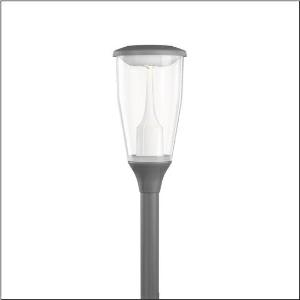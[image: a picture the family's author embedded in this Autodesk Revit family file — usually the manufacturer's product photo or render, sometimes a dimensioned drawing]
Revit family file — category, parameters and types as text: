
# Revit family: dl_11_iq___p1_0a_5xa5575nf14h000022_259a
name_source: partatom
category: Lighting Fixtures
units: mm (PartAtom-declared; Revit-internal decimal feet)

## family parameters
Cut with Voids When Loaded = No
Host = Face
Light Source = No
Part Type = Normal
Room Calculation Point = No
Round Connector Dimension = Use Diameter
Shared = No

## types (1)
- --- (1 x LED, 1530 lm, 11.8 W, 2700K)
    Apparent Load = 12 VA
    CIE Flux Codes = 34 63 91 95 100
    Color Rendering = 70
    Color Temperature = 2700K
    Default Elevation = 1800 mm
    Description = DL 11 iQ, mast luminaire, Module 540 iQ-SR, primary light control with 3 zone facetted reflector, of plastic, silver coated, highly specular, structured, primary optical cover: cover, of PMMA, transparent, light distribution: P1.0a, light emission: direct distribution, primary light characteristic: asymmetric, installation type: post-top, LED, High Power LED, rated luminous flux: 1.560lm, luminous efficacy: 149lm/W, light colour: 727, colour temperature: 2700K, control: Street-Remote, Auto-Match, Temp-Guard, Lumen-Switch, Night-Set, Smart-Wire, Light-Fading, Desk-Remote (wireless, voltage-free reading and setting of iQ features in the workshop via application-optimized NFC function/RFID function), optimised constant luminous flux control (CLO 2.0), mains connection: 220..240V, AC, 50/60Hz, connection cable pre-assembled, cable length: 5,5m, wiring characteristics: H07RN-F, 5-core, 1.5mm², start of lifetime: 12W, end of service life: 12W, reduction: 5W, luminaire housing, upper part, of diecast aluminium, coated, Siteco® metallic grey (DB 702S), spigot size: 76mm (post-top), post-top mast mounting element, of diecast aluminium, coated, Siteco® metallic grey (DB 702S), Module 540 iQ-SR, traffic white (RAL 9016), equipment: standard, protection rating (complete): IP66, insulation class (complete): insulation class II (safety insulation), certification: CE, ENEC, ENEC+, VDE, packaging unit: 1 piece

Light Distribution: P1.0a
    Height = 665 mm
    Lamp = 1 x LED
    Lamp Light Flux = 1530 lm
    Lamp Power = 11.8 W
    Lamp count = 1
    Length = 334 mm
    Luminous efficacy = 130 lm/W
    Manufacturer = Siteco
    ModVariant = No
    Model = 5XA5575NF14H000022
    Number of Poles = 1
    OnlyDefault = Yes
    Power Factor = 1
    Product Name = DL 11 iQ | P1.0a
    Product group = mast luminaire | pylon top
    ProductGroupID = 6100
    Protection Class = Protection class II
    Protection Degree = IP 66
    RLX_Detail_Level = 1
    RLX_Emergency_Light_Flux = 0 lm
    RLX_Emergency_Type = 0
    RLX_Emergency_Type_DB = No
    RlxData = <blob elided: 104629 chars, md5=9e01b40a>
    Socket = socket
    Standby Power = 0 W
    System Light Flux = 1530 lm
    System Power = 12 W
    Type Comments = factory setting: luminous flux: 100 % | dim-lin: 254 | 472 mA
    Type Image = l_1258354.jpg
    URL = http://relux.com
    VarID = @adj_042243
    Voltage = 0 V
    Weight = 0.00 kg
    Width = 0 mm  [stored 0 ft]

note: [stored X ft] marks values corroborated as IEEE doubles in the binary element streams (Revit-internal decimal feet)

## geometry (parser evidence)
native form markers: Blend x4, Sweep x9
no freeform markers — native parametric forms only
